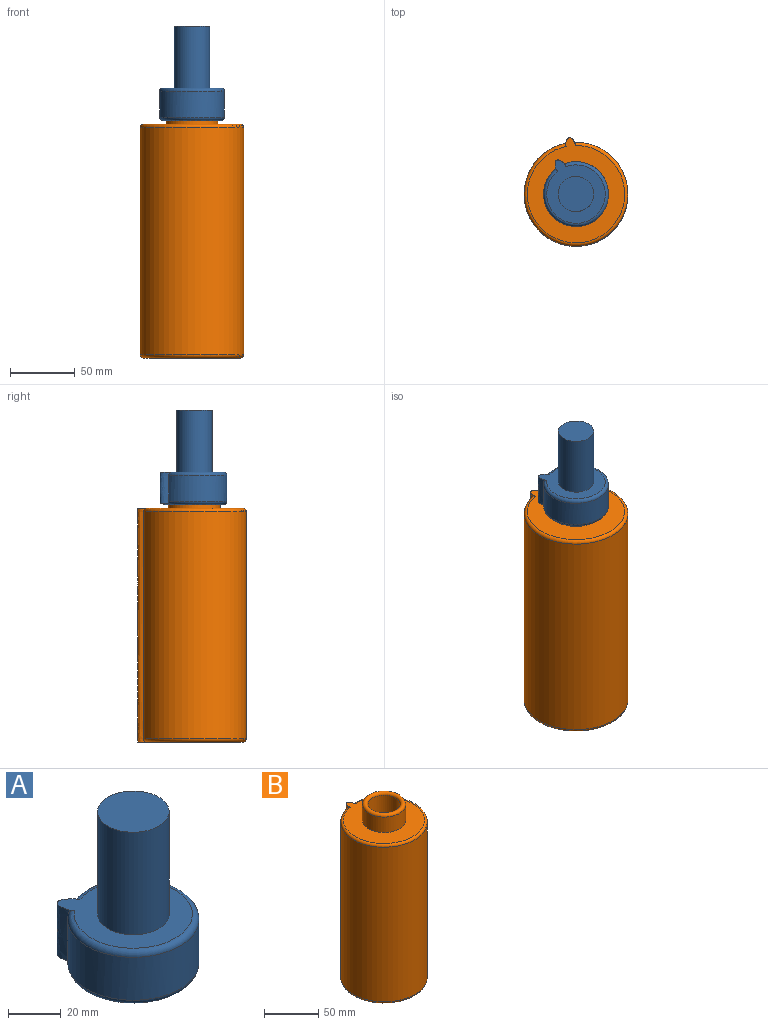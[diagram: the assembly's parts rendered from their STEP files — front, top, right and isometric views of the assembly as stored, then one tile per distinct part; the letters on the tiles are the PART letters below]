
ASSEMBLY  parts=2 mates=1
PART A: 10 faces, bbox 54.1x54.1x72.8 mm
  f0: cylinder r=25mm len=50mm, axis (0,0,-1), area 2995mm2, adj f1,f5,f8
  f1: torus R=22.5mm, axis (0,0,1), area 1097.5mm2, adj f0,f3,f8,f9
  f2: plane 49.24x45mm, normal (0,0,1), area 1051.8mm2, adj f5,f6,f8
  f3: cylinder r=20mm len=40mm, axis (0,0,-1), area 2199.1mm2, adj f1,f4
  f4: plane 40x40mm, normal (0,0,-1), area 1256.6mm2, adj f3
  f5: torus R=22.5mm, axis (0,0,1), area 564.7mm2, adj f0,f2,f8
  f6: cylinder r=13.63mm len=47.8mm, axis (0,0,-1), area 4094.1mm2, adj f2,f7
  f7: plane 27.26x27.26mm, normal (0,0,1), area 583.8mm2, adj f6
  f8: extruded ~24.1x8.93mm, area 332.7mm2, adj f0,f1,f2,f5,f9
  f9: plane 7.97x7.82mm, normal (0,0,-1), area 30.3mm2, adj f1,f8
PART B: 13 faces, bbox 86x87x200 mm
  f0: torus R=37.5mm, axis (0,0,1), area 936.3mm2, adj f1,f2,f11
  f1: cylinder r=40mm len=175mm, axis (0,0,-1), area 42779.7mm2, adj f0,f10,f11
  f2: plane 81.48x75mm, normal (0,0,1), area 3198.1mm2, adj f0,f4,f11
  f3: plane 81.48x75mm, normal (0,0,-1), area 4454.7mm2, adj f10,f11
  f4: cylinder r=20mm len=40mm, axis (0,0,-1), area 2199.1mm2, adj f2,f9
  f5: cylinder r=35mm len=170mm, axis (0,0,-1), area 36624.8mm2, adj f6,f7,f12
  f6: plane 70.09x70mm, normal (0,0,-1), area 3139.6mm2, adj f5,f8,f12
  f7: plane 70.09x70mm, normal (0,0,1), area 3846.5mm2, adj f5,f12
  f8: cylinder r=15mm len=30mm, axis (0,0,-1), area 2120.6mm2, adj f6,f9
  f9: torus R=17.5mm, axis (0,0,1), area 863.6mm2, adj f4,f8
  f10: torus R=37.5mm, axis (0,0,1), area 936.3mm2, adj f1,f3,f11
  f11: extruded ~180x7.59mm, area 2025.7mm2, adj f0,f1,f2,f3,f10
  f12: extruded ~170x4.45mm, area 794.4mm2, adj f5,f6,f7
PLACE A t=(8.16,36.36,172.79)mm
PLACE B t=(8.16,36.36,-10.12)mm
MATE cylindrical A.f0 <-> B.f0  axis (0,0,1) through (8.16,36.36,172.79)mm
